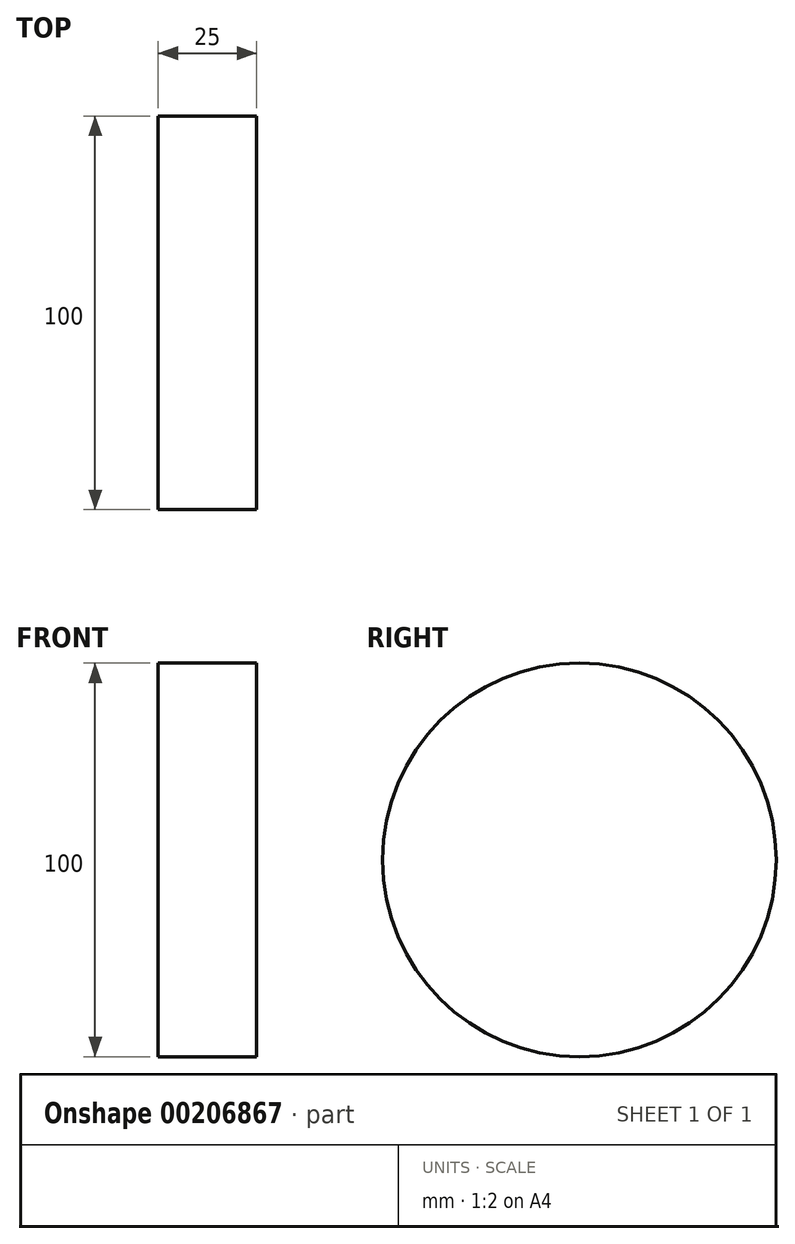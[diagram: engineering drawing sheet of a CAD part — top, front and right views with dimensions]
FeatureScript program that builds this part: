
annotation { "Feature Type Name" : "Feature", "Feature Type Description" : "" }
export const myFeature = defineFeature(function(context is Context, id is Id, definition is map)
    precondition{}
    {
        {
            var Q0;
            Q0=qCreatedBy(makeId("Right.planeOp"),FACE);
            var sketch = newSketch(context, id + "F0", { "sketchPlane" : qUnion([Q0])});
            skCircle(sketch, "E0", {"center": v(0, 0) * mm, "radius": 50 * mm});
            skLineSegment(sketch, "E1", {"start": v(0, 50) * mm, "end": v(-24.42, -23.93) * mm});
            skLineSegment(sketch, "E2", {"start": v(-24.42, -23.93) * mm, "end": v(-47.24, -16.4) * mm});
            skSolve(sketch);
        }
        {
            var Q0;
            {var subQ0=sQuery(id+"F0.wireOp",EDGE,"E1");Q0=makeQuery(id+"F0.imprint","IMPRINT",FACE,{"disambiguationData":[TD([[makeQuery(id+"F0.imprint","IMPRINT",EDGE,{"derivedFrom":subQ0}),1.0]])]});}
            var Q1;
            {var subQ0=sQuery(id+"F0.wireOp",EDGE,"E1");Q1=makeQuery(id+"F0.imprint","IMPRINT",FACE,{"disambiguationData":[TD([[makeQuery(id+"F0.imprint","IMPRINT",EDGE,{"derivedFrom":subQ0}),-1.0]])]});}
            extrude(context, id + "F1", {"entities" : qUnion([Q0, Q1]), "depth" : 25 * mm});
        }
    });
